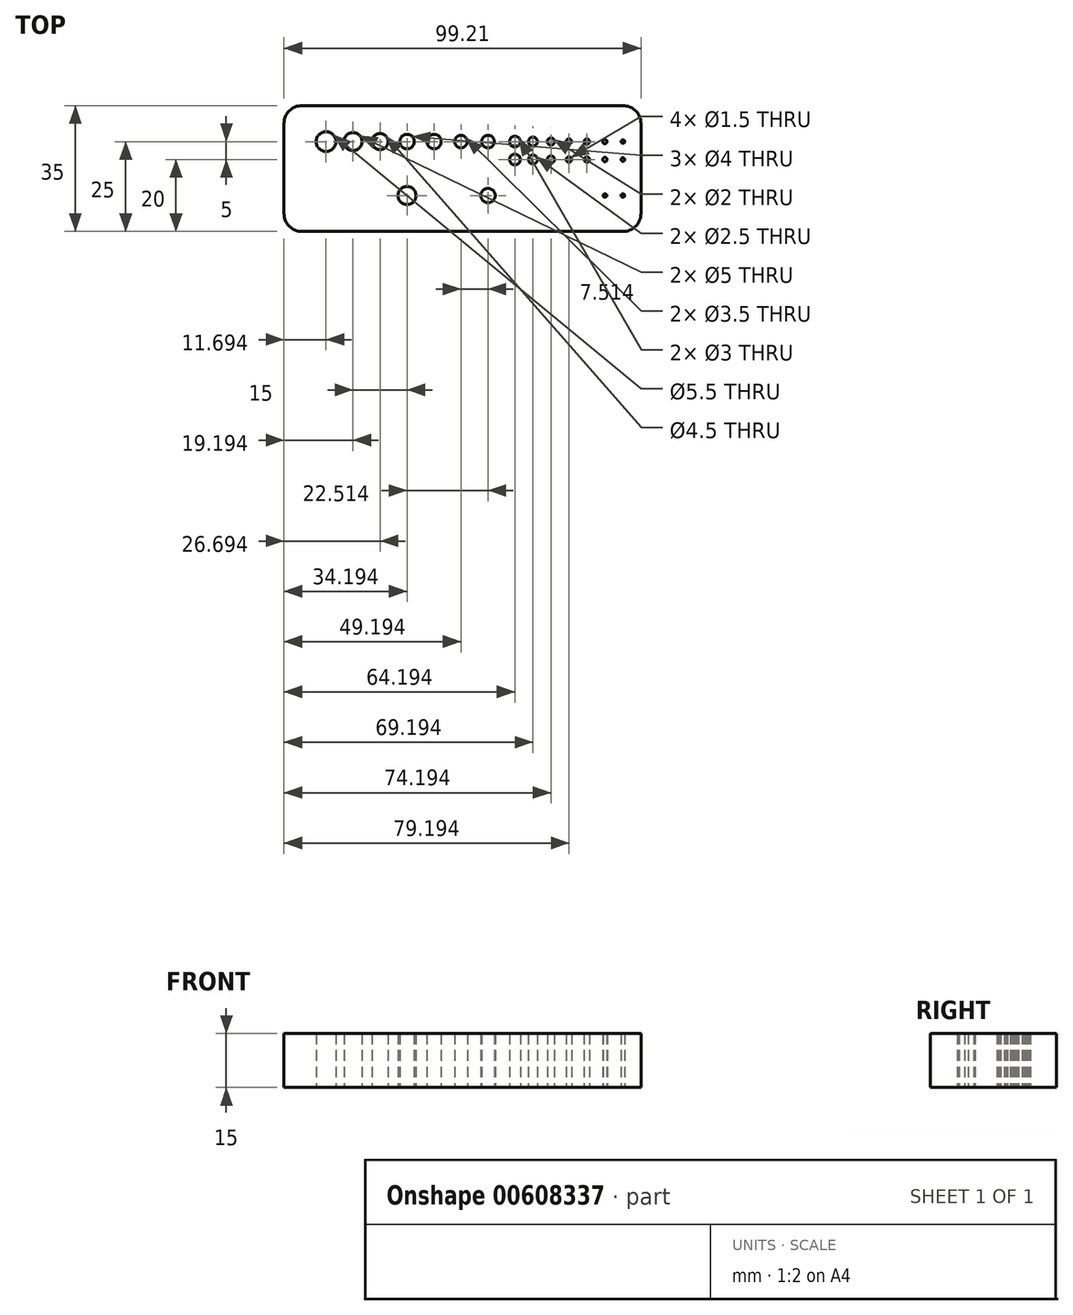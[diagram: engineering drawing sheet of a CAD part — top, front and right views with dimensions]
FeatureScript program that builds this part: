
annotation { "Feature Type Name" : "Feature", "Feature Type Description" : "" }
export const myFeature = defineFeature(function(context is Context, id is Id, definition is map)
    precondition{}
    {
        {
            var Q0;
            Q0=qCreatedBy(makeId("Top.planeOp"),FACE);
            var sketch = newSketch(context, id + "F0", { "sketchPlane" : qUnion([Q0])});
            skLineSegment(sketch, "E0.bottom", {"start": v(59.65, -10) * mm, "end": v(-30.35, -10) * mm});
            skLineSegment(sketch, "E0.top", {"start": v(59.65, 25) * mm, "end": v(-39.56, 25) * mm});
            skLineSegment(sketch, "E0.left", {"start": v(59.65, -10) * mm, "end": v(59.65, 25) * mm});
            skPoint(sketch, "E0.middle", {"position": v(0, 0) * mm});
            skLineSegment(sketch, "E1", {"start": v(59.65, 15) * mm, "end": v(-39.56, 15) * mm, "construction": true});
            skLineSegment(sketch, "E2", {"start": v(59.65, 10) * mm, "end": v(-39.56, 10) * mm, "construction": true});
            skLineSegment(sketch, "E3", {"start": v(54.65, 25) * mm, "end": v(54.65, -10) * mm, "construction": true});
            skLineSegment(sketch, "E4.1.0.0", {"start": v(49.65, 24.95) * mm, "end": v(49.65, -10) * mm, "construction": true});
            skLineSegment(sketch, "E4.2.0.0", {"start": v(44.63, 24.95) * mm, "end": v(44.63, -10.05) * mm, "construction": true});
            skLineSegment(sketch, "E4.3.0.0", {"start": v(39.63, 25) * mm, "end": v(39.63, -13.47) * mm, "construction": true});
            skLineSegment(sketch, "E4.4.0.0", {"start": v(34.63, 25) * mm, "end": v(34.63, -10.05) * mm, "construction": true});
            skLineSegment(sketch, "E4.5.0.0", {"start": v(29.63, 25) * mm, "end": v(29.63, -10.05) * mm, "construction": true});
            skLineSegment(sketch, "E4.6.0.0", {"start": v(24.63, 25) * mm, "end": v(24.63, -10.05) * mm, "construction": true});
            skLineSegment(sketch, "E4.9.0.0", {"start": v(9.63, 24.95) * mm, "end": v(9.63, -10.05) * mm, "construction": true});
            skLineSegment(sketch, "E4.12.0.0", {"start": v(-5.37, 24.95) * mm, "end": v(-5.37, -24.95) * mm, "construction": true});
            skLineSegment(sketch, "E4.15.0.0", {"start": v(-20.37, 24.95) * mm, "end": v(-20.37, -10.05) * mm, "construction": true});
            skLineSegment(sketch, "E4.18.0.0", {"start": v(-39.56, 25) * mm, "end": v(-39.56, -10) * mm});
            skLineSegment(sketch, "E4.direction1", {"start": v(54.65, -10) * mm, "end": v(49.65, -10) * mm, "construction": true});
            skCircle(sketch, "E5", {"center": v(54.65, 15) * mm, "radius": 0.5 * mm});
            skCircle(sketch, "E6", {"center": v(54.65, 10) * mm, "radius": 0.5 * mm});
            skCircle(sketch, "E7.1.0.0", {"center": v(49.65, 10) * mm, "radius": 0.6 * mm});
            skCircle(sketch, "E7.1.0.1", {"center": v(49.62, 15) * mm, "radius": 0.6 * mm});
            skCircle(sketch, "E7.2.0.1", {"center": v(44.63, 10) * mm, "radius": 0.75 * mm});
            skCircle(sketch, "E7.3.0.1", {"center": v(39.63, 10) * mm, "radius": 0.75 * mm});
            skCircle(sketch, "E7.4.0.1", {"center": v(34.63, 10) * mm, "radius": 1 * mm});
            skCircle(sketch, "E7.5.0.1", {"center": v(29.63, 10) * mm, "radius": 1.25 * mm});
            skLineSegment(sketch, "E7.direction1", {"start": v(54.65, 10) * mm, "end": v(49.65, 10) * mm, "construction": true});
            skCircle(sketch, "E8", {"center": v(24.63, 15) * mm, "radius": 1.5 * mm});
            skCircle(sketch, "E9", {"center": v(24.63, 10) * mm, "radius": 1.5 * mm});
            skCircle(sketch, "E10", {"center": v(17.15, 15) * mm, "radius": 1.75 * mm});
            skCircle(sketch, "E11", {"center": v(9.63, 15) * mm, "radius": 1.75 * mm});
            skCircle(sketch, "E12", {"center": v(2.13, 15) * mm, "radius": 2 * mm});
            skCircle(sketch, "E13", {"center": v(-5.37, 15) * mm, "radius": 2 * mm});
            skCircle(sketch, "E14", {"center": v(-12.87, 15) * mm, "radius": 2.25 * mm});
            skCircle(sketch, "E15", {"center": v(-20.37, 15) * mm, "radius": 2.5 * mm});
            skCircle(sketch, "E16", {"center": v(-27.87, 15) * mm, "radius": 2.75 * mm});
            skCircle(sketch, "E17", {"center": v(17.15, 0) * mm, "radius": 2 * mm});
            skCircle(sketch, "E18", {"center": v(-5.37, 0) * mm, "radius": 2.5 * mm});
            skLineSegment(sketch, "E19", {"start": v(-30.35, -10) * mm, "end": v(-39.56, -10) * mm});
            skCircle(sketch, "E20", {"center": v(29.63, 15) * mm, "radius": 1.25 * mm});
            skCircle(sketch, "E21", {"center": v(34.63, 15) * mm, "radius": 1 * mm});
            skCircle(sketch, "E22", {"center": v(44.63, 15) * mm, "radius": 0.75 * mm});
            skCircle(sketch, "E23", {"center": v(39.63, 15) * mm, "radius": 0.75 * mm});
            skLineSegment(sketch, "E24", {"start": v(17.15, 25) * mm, "end": v(17.15, 0) * mm, "construction": true});
            skCircle(sketch, "E25", {"center": v(54.65, 0) * mm, "radius": 0.5 * mm});
            skCircle(sketch, "E26", {"center": v(49.65, 0) * mm, "radius": 0.5 * mm});
            skLineSegment(sketch, "E27.bottom", {"start": v(-42.06, 27.5) * mm, "end": v(62.15, 27.5) * mm});
            skLineSegment(sketch, "E27.top", {"start": v(-42.06, -12.5) * mm, "end": v(62.15, -12.5) * mm});
            skLineSegment(sketch, "E27.left", {"start": v(-42.06, 27.5) * mm, "end": v(-42.06, -12.5) * mm});
            skLineSegment(sketch, "E27.right", {"start": v(62.15, 27.5) * mm, "end": v(62.15, -12.5) * mm});
            skLineSegment(sketch, "E28.trimOffspring", {"start": v(-25.35, -10) * mm, "end": v(-25.35, -10.5) * mm, "construction": true});
            skSolve(sketch);
        }
        {
            var Q0;
            Q0=makeQuery(id+"F0.imprint","IMPRINT",FACE,{"disambiguationData":[TD([[makeQuery(id+"F0.imprint","IMPRINT",EDGE,{"derivedFrom":sQuery(id+"F0.wireOp",EDGE,"E0.bottom")}),-1.0]])]});
            extrude(context, id + "F1", {"entities" : qUnion([Q0]), "depth" : 15 * mm, "offsetDistance" : 25 * mm});
        }
        {
            var Q0;
            Q0=makeQuery(id+"F1.opExtrude","SWEPT_EDGE",EDGE,{"disambiguationData":[OSD([sQuery(id+"F0.wireOp",EDGE,"E0.top"),sQuery(id+"F0.wireOp",EDGE,"E4.18.0.0")])]});
            var Q1;
            Q1=makeQuery(id+"F1.opExtrude","SWEPT_EDGE",EDGE,{"disambiguationData":[OSD([sQuery(id+"F0.wireOp",EDGE,"E4.18.0.0"),sQuery(id+"F0.wireOp",EDGE,"E19")])]});
            var Q2;
            Q2=makeQuery(id+"F1.opExtrude","SWEPT_EDGE",EDGE,{"disambiguationData":[OSD([sQuery(id+"F0.wireOp",EDGE,"E0.bottom"),sQuery(id+"F0.wireOp",EDGE,"E0.left")])]});
            var Q3;
            Q3=makeQuery(id+"F1.opExtrude","SWEPT_EDGE",EDGE,{"disambiguationData":[OSD([sQuery(id+"F0.wireOp",EDGE,"E0.top"),sQuery(id+"F0.wireOp",EDGE,"E0.left")])]});
            fillet(context, id + "F2", {"entities" : qUnion([Q0, Q1, Q2, Q3]), "tangentPropagation" : true, "radius" : 5 * mm, "defaultsChanged" : false, "vertexSettings" : [], "allowEdgeOverflow" : false});
        }
    });
